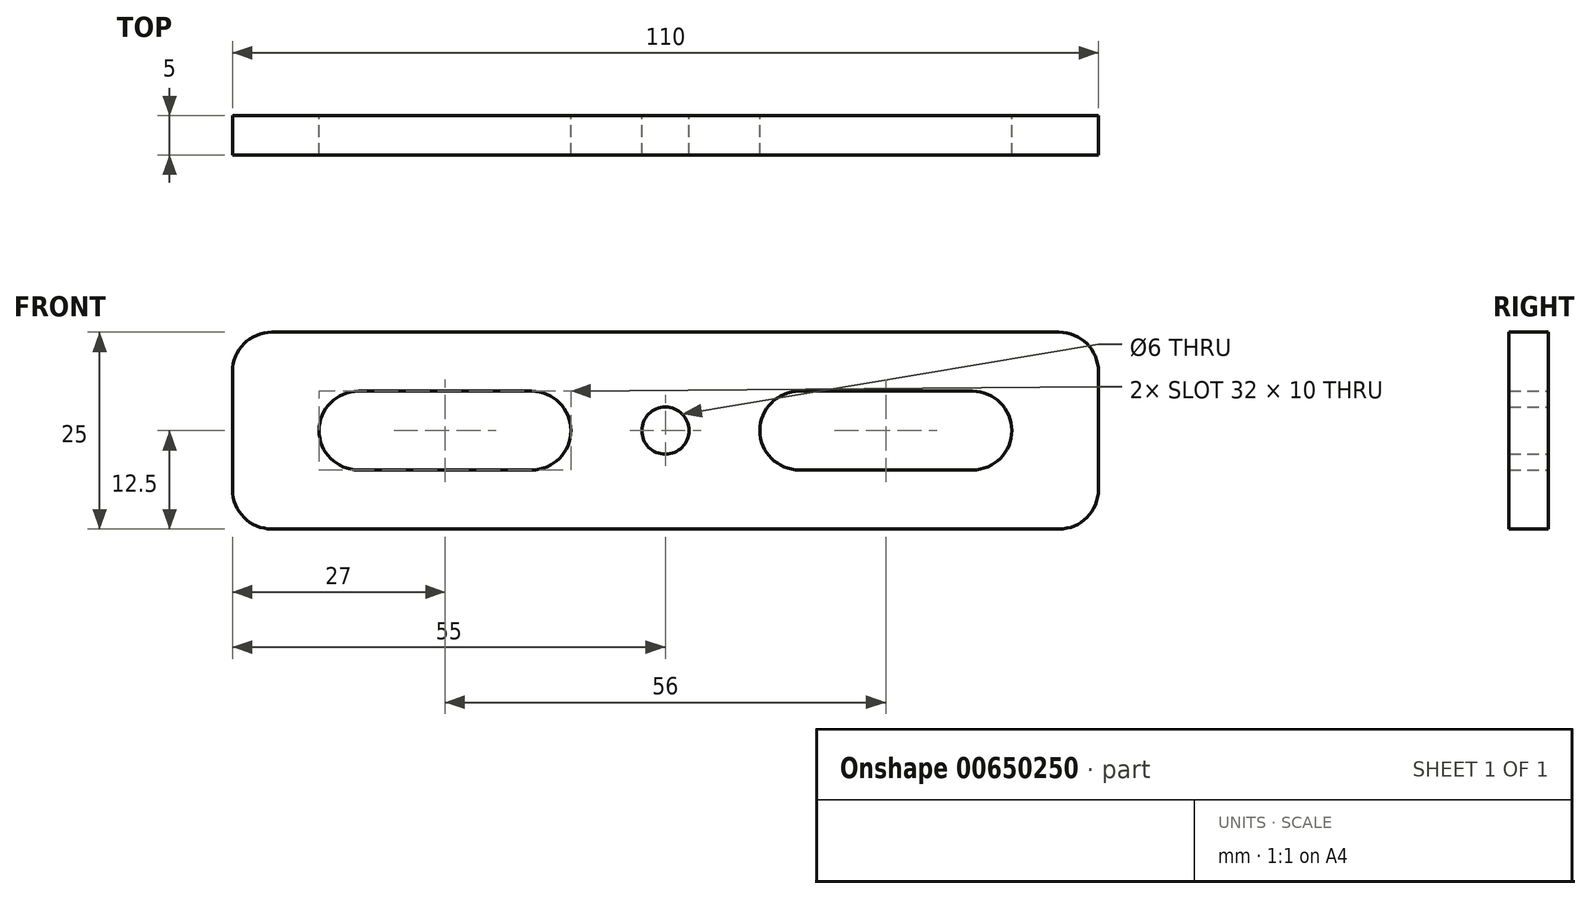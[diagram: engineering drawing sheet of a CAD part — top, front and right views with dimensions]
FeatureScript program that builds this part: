
annotation { "Feature Type Name" : "Feature", "Feature Type Description" : "" }
export const myFeature = defineFeature(function(context is Context, id is Id, definition is map)
    precondition{}
    {
        {
            var Q0;
            Q0=qCreatedBy(makeId("Front.planeOp"),FACE);
            var sketch = newSketch(context, id + "F0", { "sketchPlane" : qUnion([Q0])});
            skLineSegment(sketch, "E0.bottom", {"start": v(-50, 12.5) * mm, "end": v(50, 12.5) * mm});
            skLineSegment(sketch, "E0.top", {"start": v(-50, -12.5) * mm, "end": v(50, -12.5) * mm});
            skLineSegment(sketch, "E0.left", {"start": v(-55, 7.5) * mm, "end": v(-55, -7.5) * mm});
            skLineSegment(sketch, "E0.right", {"start": v(55, 7.5) * mm, "end": v(55, -7.5) * mm});
            skPoint(sketch, "E0.middle", {"position": v(0, 0) * mm});
            skLineSegment(sketch, "E1", {"start": v(-55, 0) * mm, "end": v(55, 0) * mm, "construction": true});
            skLineSegment(sketch, "E2", {"start": v(-44, 0) * mm, "end": v(-44, 0) * mm});
            skLineSegment(sketch, "E3", {"start": v(44, 0) * mm, "end": v(44, 0) * mm});
            skLineSegment(sketch, "E4", {"start": v(12, 0) * mm, "end": v(12, 0) * mm});
            skLineSegment(sketch, "E5.bottom", {"start": v(12, 0) * mm, "end": v(44, 0) * mm});
            skLineSegment(sketch, "E5.top", {"start": v(12, 0) * mm, "end": v(44, 0) * mm});
            skLineSegment(sketch, "E6", {"start": v(-12, 0) * mm, "end": v(-12, 0) * mm});
            skLineSegment(sketch, "E7", {"start": v(17, 5) * mm, "end": v(39, 5) * mm});
            skLineSegment(sketch, "E8", {"start": v(17, -5) * mm, "end": v(39, -5) * mm});
            skPoint(sketch, "E9.newPointB", {"position": v(44, 12.5) * mm});
            skArc(sketch, "E9.filletArc", {"start": v(44, 0) * mm, "mid": v(42.54, 3.54) * mm, "end": v(39, 5) * mm});
            skPoint(sketch, "E10.newPointA", {"position": v(44, -12.5) * mm});
            skArc(sketch, "E10.filletArc", {"start": v(39, -5) * mm, "mid": v(42.54, -3.54) * mm, "end": v(44, 0) * mm});
            skPoint(sketch, "E11.newPointB", {"position": v(12, -12.5) * mm});
            skArc(sketch, "E11.filletArc", {"start": v(12, 0) * mm, "mid": v(13.46, -3.54) * mm, "end": v(17, -5) * mm});
            skPoint(sketch, "E12.newPointA", {"position": v(12, 12.5) * mm});
            skArc(sketch, "E12.filletArc", {"start": v(17, 5) * mm, "mid": v(13.46, 3.54) * mm, "end": v(12, 0) * mm});
            skLineSegment(sketch, "E13", {"start": v(-39, 5) * mm, "end": v(-17, 5) * mm});
            skLineSegment(sketch, "E14", {"start": v(-39, -5) * mm, "end": v(-17, -5) * mm});
            skPoint(sketch, "E15.newPointA", {"position": v(-12, 5) * mm});
            skPoint(sketch, "E15.newPointB", {"position": v(-12, 12.5) * mm});
            skArc(sketch, "E15.filletArc", {"start": v(-12, 0) * mm, "mid": v(-13.46, 3.54) * mm, "end": v(-17, 5) * mm});
            skPoint(sketch, "E16.newPointB", {"position": v(-12, -5) * mm});
            skArc(sketch, "E16.filletArc", {"start": v(-17, -5) * mm, "mid": v(-13.46, -3.54) * mm, "end": v(-12, 0) * mm});
            skPoint(sketch, "E17.newPointB", {"position": v(-44, 12.5) * mm});
            skArc(sketch, "E17.filletArc", {"start": v(-39, 5) * mm, "mid": v(-42.54, 3.54) * mm, "end": v(-44, 0) * mm});
            skArc(sketch, "E18.filletArc", {"start": v(-44, 0) * mm, "mid": v(-42.54, -3.54) * mm, "end": v(-39, -5) * mm});
            skCircle(sketch, "E19", {"center": v(0, 0) * mm, "radius": 3 * mm});
            skPoint(sketch, "E20.visualSharp", {"position": v(-55, 12.5) * mm});
            skArc(sketch, "E20.filletArc", {"start": v(-50, 12.5) * mm, "mid": v(-53.54, 11.04) * mm, "end": v(-55, 7.5) * mm});
            skPoint(sketch, "E21.visualSharp", {"position": v(-55, -12.5) * mm});
            skArc(sketch, "E21.filletArc", {"start": v(-55, -7.5) * mm, "mid": v(-53.54, -11.04) * mm, "end": v(-50, -12.5) * mm});
            skPoint(sketch, "E22.visualSharp", {"position": v(55, -12.5) * mm});
            skArc(sketch, "E22.filletArc", {"start": v(50, -12.5) * mm, "mid": v(53.54, -11.04) * mm, "end": v(55, -7.5) * mm});
            skPoint(sketch, "E23.visualSharp", {"position": v(55, 12.5) * mm});
            skArc(sketch, "E23.filletArc", {"start": v(55, 7.5) * mm, "mid": v(53.54, 11.04) * mm, "end": v(50, 12.5) * mm});
            skSolve(sketch);
        }
        {
            var Q0;
            Q0=makeQuery(id+"F0.imprint","IMPRINT",FACE,{"disambiguationData":[TD([[makeQuery(id+"F0.imprint","IMPRINT",EDGE,{"derivedFrom":sQuery(id+"F0.wireOp",EDGE,"E0.bottom")}),-1.0]])]});
            extrude(context, id + "F1", {"entities" : qUnion([Q0]), "depth" : 5 * mm, "offsetDistance" : 25 * mm});
        }
    });
